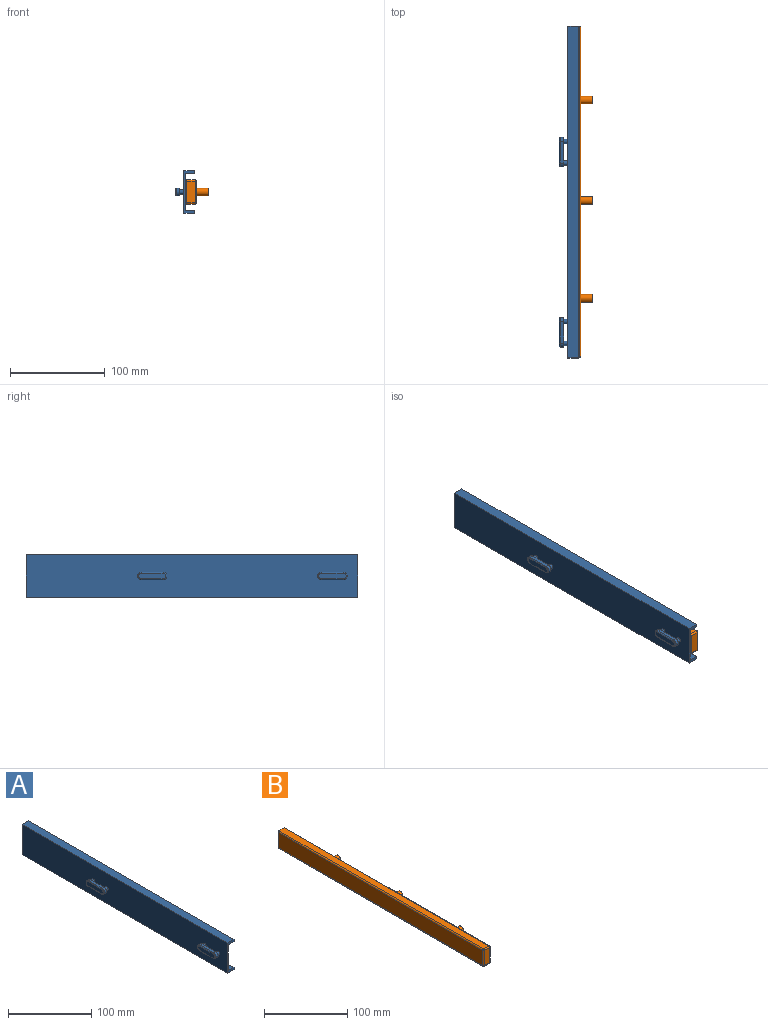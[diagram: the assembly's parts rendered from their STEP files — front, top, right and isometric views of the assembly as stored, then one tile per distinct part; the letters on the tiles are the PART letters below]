
ASSEMBLY  parts=2 mates=1
PART A: 34 faces, bbox 20.1x350x44.5 mm
  f0: plane 350x3.18mm, normal (1,0,0), area 1111.2mm2, adj f1,f2,f3,f7
  f1: plane 44.45x11.11mm, normal (0,-1,0), area 130.1mm2, adj f0,f2,f4,f5,f6,f7,f8,f9
  f2: plane 350x11.11mm, normal (0,0,-1), area 3889.4mm2, adj f0,f1,f3,f6
  f3: plane 44.45x11.11mm, normal (0,1,0), area 130.1mm2, adj f0,f2,f4,f5,f6,f7,f8,f9
  f4: plane 350x11.11mm, normal (0,0,1), area 3889.4mm2, adj f1,f3,f5,f6
  f5: plane 350x3.18mm, normal (1,0,0), area 1111.3mm2, adj f1,f3,f4,f8
  f6: plane 350x44.45mm, normal (-1,0,0), area 15486.6mm2, adj f1,f2,f3,f4,f10,f11,f12,f13
  f7: plane 350x9.55mm, normal (0,0,1), area 3342.6mm2, adj f0,f1,f3,f9
  f8: plane 350x9.55mm, normal (0,0,-1), area 3342.6mm2, adj f1,f3,f5,f9
  f9: plane 350x38.1mm, normal (1,0,0), area 13335mm2, adj f1,f3,f7,f8
  f10: cylinder r=2.37mm len=4.75mm, axis (1,0,0), area 67.1mm2, adj f6,f19
  f11: cylinder r=2.37mm len=4.75mm, axis (1,0,0), area 67.1mm2, adj f6,f19
  f12: cylinder r=2.37mm len=4.75mm, axis (1,0,0), area 67.1mm2, adj f6,f25
  f13: cylinder r=2.37mm len=4.75mm, axis (1,0,0), area 67.1mm2, adj f6,f25
  f14: cylinder r=4mm len=8mm, axis (1,0,0), area 43.8mm2, adj f15,f17,f19,f31
  f15: plane 23x3.48mm, normal (0,0,-1), area 80.1mm2, adj f14,f16,f19,f30
  f16: cylinder r=4mm len=8mm, axis (1,0,0), area 43.8mm2, adj f15,f17,f19,f32
  f17: plane 23x3.48mm, normal (0,0,1), area 80.1mm2, adj f14,f16,f19,f33
  f18: plane 28.97x5.97mm, normal (-1,0,0), area 165.2mm2, adj f30,f31,f32,f33
  f19: plane 31x8mm, normal (1,0,0), area 198.8mm2, adj f10,f11,f14,f15,f16,f17
  f20: plane 23x3.48mm, normal (0,0,1), area 80.1mm2, adj f21,f23,f25,f29
  f21: cylinder r=4mm len=8mm, axis (1,0,0), area 43.8mm2, adj f20,f22,f25,f27
  f22: plane 23x3.48mm, normal (0,0,-1), area 80.1mm2, adj f21,f23,f25,f26
  f23: cylinder r=4mm len=8mm, axis (1,0,0), area 43.8mm2, adj f20,f22,f25,f28
  f24: plane 28.97x5.97mm, normal (-1,0,0), area 165.2mm2, adj f26,f27,f28,f29
  f25: plane 31x8mm, normal (1,0,0), area 198.8mm2, adj f12,f13,f20,f21,f22,f23
  f26: cylinder r=1.02mm len=23mm, axis (0,1,0), area 36.7mm2, adj f22,f24,f27,f28
  f27: torus R=2.98mm, axis (-1,0,0), area 18.2mm2, adj f21,f24,f26,f29
  f28: torus R=2.98mm, axis (-1,0,0), area 18.2mm2, adj f23,f24,f26,f29
  f29: cylinder r=1.02mm len=23mm, axis (0,-1,0), area 36.7mm2, adj f20,f24,f27,f28
  f30: cylinder r=1.02mm len=23mm, axis (0,1,0), area 36.7mm2, adj f15,f18,f31,f32
  f31: torus R=2.98mm, axis (-1,0,0), area 18.2mm2, adj f14,f18,f30,f33
  f32: torus R=2.98mm, axis (-1,0,0), area 18.2mm2, adj f16,f18,f30,f33
  f33: cylinder r=1.02mm len=23mm, axis (0,-1,0), area 36.7mm2, adj f17,f18,f31,f32
PART B: 24 faces, bbox 24.6x350x25.4 mm
  f0: plane 348.43x8.76mm, normal (0,0,-1), area 3053.3mm2, adj f1,f12,f13,f14
  f1: plane 25.4x11.91mm, normal (0,1,0), area 300.5mm2, adj f0,f2,f4,f5,f12,f14,f17,f20
  f2: plane 348.43x8.76mm, normal (0,0,1), area 3053.3mm2, adj f1,f17,f20,f23
  f3: plane 22.25x8.76mm, normal (0,-1,0), area 195mm2, adj f13,f18,f19,f23
  f4: plane 348.43x22.25mm, normal (1,0,0), area 7601.8mm2, adj f1,f6,f8,f10,f12,f17,f18
  f5: plane 348.43x22.25mm, normal (-1,0,0), area 7752.6mm2, adj f1,f14,f19,f20
  f6: cylinder r=4mm len=12.7mm, axis (-1,0,0), area 319.2mm2, adj f4,f7
  f7: plane 8x8mm, normal (1,0,0), area 50.3mm2, adj f6
  f8: cylinder r=4mm len=12.7mm, axis (-1,0,0), area 319.2mm2, adj f4,f9
  f9: plane 8x8mm, normal (1,0,0), area 50.3mm2, adj f8
  f10: cylinder r=4mm len=12.7mm, axis (-1,0,0), area 319.2mm2, adj f4,f11
  f11: plane 8x8mm, normal (1,0,0), area 50.3mm2, adj f10
  f12: cylinder r=1.57mm len=348.43mm, axis (0,-1,0), area 861.9mm2, adj f0,f1,f4,f15
  f13: cylinder r=1.57mm len=8.76mm, axis (-1,0,0), area 21.7mm2, adj f0,f3,f15,f16
  f14: cylinder r=1.57mm len=348.43mm, axis (0,1,0), area 861.9mm2, adj f0,f1,f5,f16
  f15: sphere r=1.57mm, area 3.9mm2, adj f12,f13,f18
  f16: sphere r=1.57mm, area 3.9mm2, adj f13,f14,f19
  f17: cylinder r=1.57mm len=348.43mm, axis (0,1,0), area 861.9mm2, adj f1,f2,f4,f21
  f18: cylinder r=1.57mm len=22.25mm, axis (0,0,1), area 55mm2, adj f3,f4,f15,f21
  f19: cylinder r=1.57mm len=22.25mm, axis (0,0,-1), area 55mm2, adj f3,f5,f16,f22
  f20: cylinder r=1.57mm len=348.43mm, axis (0,-1,0), area 861.9mm2, adj f1,f2,f5,f22
  f21: sphere r=1.57mm, area 3.9mm2, adj f17,f18,f23
  f22: sphere r=1.57mm, area 3.9mm2, adj f19,f20,f23
  f23: cylinder r=1.57mm len=8.76mm, axis (1,0,0), area 21.7mm2, adj f2,f3,f21,f22
PLACE A t=(-96.6,-40.63,21.79)mm fixed
PLACE B t=(-95.03,-40.63,21.79)mm
MATE fastened B.f5 <-> A.f9  axis (-1,0,0) through (-95.03,121.67,21.79)mm
